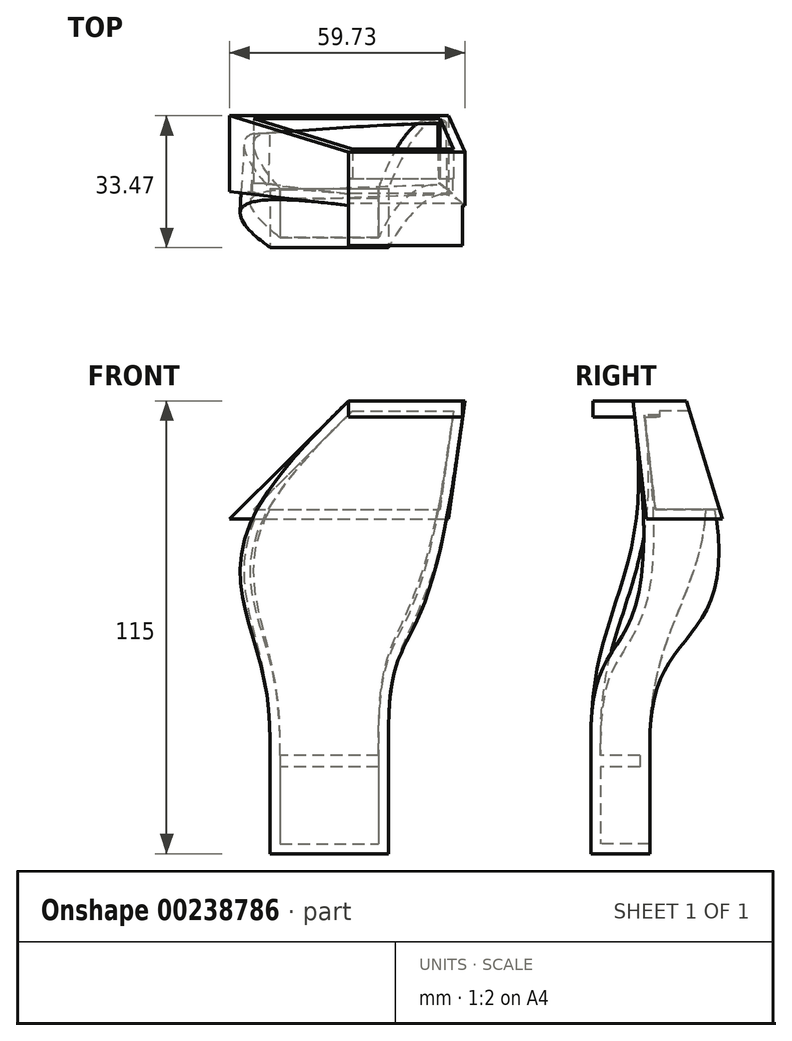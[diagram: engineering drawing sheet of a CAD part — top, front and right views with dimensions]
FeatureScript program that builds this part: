
annotation { "Feature Type Name" : "Feature", "Feature Type Description" : "" }
export const myFeature = defineFeature(function(context is Context, id is Id, definition is map)
    precondition{}
    {
        {
            var Q0;
            Q0=qCreatedBy(makeId("Top.planeOp"),FACE);
            var sketch = newSketch(context, id + "F0", { "sketchPlane" : qUnion([Q0])});
            skLineSegment(sketch, "E0.bottom", {"start": v(-29.41, -2.5) * mm, "end": v(0.59, -2.5) * mm});
            skLineSegment(sketch, "E0.top", {"start": v(-29.41, -17.5) * mm, "end": v(0.59, -17.5) * mm});
            skLineSegment(sketch, "E0.left", {"start": v(-29.41, -2.5) * mm, "end": v(-29.41, -17.5) * mm});
            skLineSegment(sketch, "E0.right", {"start": v(0.59, -2.5) * mm, "end": v(0.59, -17.5) * mm});
            skSolve(sketch);
        }
        {
            var Q0;
            Q0=makeQuery(id+"F0.imprint","IMPRINT",FACE,{"disambiguationData":[TD([[makeQuery(id+"F0.imprint","IMPRINT",EDGE,{"derivedFrom":sQuery(id+"F0.wireOp",EDGE,"E0.bottom")}),-1.0]])]});
            extrude(context, id + "F1", {"entities" : qUnion([Q0]), "depth" : 25 * mm});
        }
        {
            var Q0;
            Q0=makeQuery(id+"F1.opExtrude","CAP_FACE",FACE,{"disambiguationData":[OSD([sQuery(id+"F0.wireOp",EDGE,"E0.bottom"),sQuery(id+"F0.wireOp",EDGE,"E0.top"),sQuery(id+"F0.wireOp",EDGE,"E0.left"),sQuery(id+"F0.wireOp",EDGE,"E0.right")])],"isStart":false});
            cPlane(context, id + "F2", {"entities" : qUnion([Q0]), "cplaneType" : CPlaneType.OFFSET, "offset" : 90 * mm, "width" : 150 * mm, "height" : 150 * mm});
        }
        {
            var Q0;
            Q0=qCreatedBy(id+"F2.planeOp",FACE);
            var sketch = newSketch(context, id + "F3", { "sketchPlane" : qUnion([Q0])});
            skLineSegment(sketch, "E1.bottom", {"start": v(-9.57, 6.8) * mm, "end": v(20.02, 6.8) * mm});
            skLineSegment(sketch, "E1.top", {"start": v(-9.57, -6.78) * mm, "end": v(20.02, -6.78) * mm});
            skLineSegment(sketch, "E1.left", {"start": v(-9.57, 6.8) * mm, "end": v(-9.57, -6.78) * mm});
            skLineSegment(sketch, "E1.right", {"start": v(20.02, 6.8) * mm, "end": v(20.02, -6.78) * mm});
            skSolve(sketch);
        }
        {
            var Q0;
            Q0=makeQuery(id+"F3.imprint","IMPRINT",FACE,{"disambiguationData":[TD([[makeQuery(id+"F3.imprint","IMPRINT",EDGE,{"derivedFrom":sQuery(id+"F3.wireOp",EDGE,"E1.bottom")}),-1.0]])]});
            cPlane(context, id + "F4", {"entities" : qUnion([Q0]), "cplaneType" : CPlaneType.OFFSET, "offset" : 30 * mm, "oppositeDirection" : true, "width" : 150 * mm, "height" : 150 * mm});
        }
        {
            var Q0;
            Q0=qCreatedBy(id+"F4.planeOp",FACE);
            var sketch = newSketch(context, id + "F5", { "sketchPlane" : qUnion([Q0])});
            skLineSegment(sketch, "E2.bottom", {"start": v(-39.71, 15.96) * mm, "end": v(15.91, 15.96) * mm});
            skLineSegment(sketch, "E2.top", {"start": v(-39.71, -3.35) * mm, "end": v(15.91, -3.35) * mm});
            skLineSegment(sketch, "E2.left", {"start": v(-39.71, 15.96) * mm, "end": v(-39.71, -3.35) * mm});
            skLineSegment(sketch, "E2.right", {"start": v(15.91, 15.96) * mm, "end": v(15.91, -3.35) * mm});
            skSolve(sketch);
        }
        {
            var Q0;
            Q0=makeQuery(id+"F3.imprint","IMPRINT",FACE,{"disambiguationData":[TD([[makeQuery(id+"F3.imprint","IMPRINT",EDGE,{"derivedFrom":sQuery(id+"F3.wireOp",EDGE,"E1.bottom")}),-1.0]])]});
            var Q1;
            Q1=makeQuery(id+"F5.imprint","IMPRINT",FACE,{"disambiguationData":[TD([[makeQuery(id+"F5.imprint","IMPRINT",EDGE,{"derivedFrom":sQuery(id+"F5.wireOp",EDGE,"E2.bottom")}),-1.0]])]});
            loft(context, id + "F6", {"sheetProfilesArray" : [{ "sheetProfileEntities" : qUnion([Q0]) }, { "sheetProfileEntities" : qUnion([Q1]) }]});
        }
        {
            var Q0;
            Q0=makeQuery(id+"F6.opLoft","CAP_FACE",FACE,{"disambiguationData":[OSD([makeQuery(id+"F3.imprint","IMPRINT",FACE,{"disambiguationData":[TD([[makeQuery(id+"F3.imprint","IMPRINT",EDGE,{"derivedFrom":sQuery(id+"F3.wireOp",EDGE,"E1.bottom")}),-1.0]])]})])],"isStart":true});
            var Q1;
            Q1=makeQuery(id+"F1.opExtrude","CAP_FACE",FACE,{"disambiguationData":[OSD([sQuery(id+"F0.wireOp",EDGE,"E0.bottom"),sQuery(id+"F0.wireOp",EDGE,"E0.top"),sQuery(id+"F0.wireOp",EDGE,"E0.left"),sQuery(id+"F0.wireOp",EDGE,"E0.right")])],"isStart":false});
            var Q2;
            Q2=makeQuery(id+"F1.opExtrude","CAP_FACE",FACE,{"disambiguationData":[OSD([sQuery(id+"F0.wireOp",EDGE,"E0.bottom"),sQuery(id+"F0.wireOp",EDGE,"E0.top"),sQuery(id+"F0.wireOp",EDGE,"E0.left"),sQuery(id+"F0.wireOp",EDGE,"E0.right")])],"isStart":false});
            var Q3;
            Q3=makeQuery(id+"F6.opLoft","CAP_FACE",FACE,{"disambiguationData":[OSD([makeQuery(id+"F3.imprint","IMPRINT",FACE,{"disambiguationData":[TD([[makeQuery(id+"F3.imprint","IMPRINT",EDGE,{"derivedFrom":sQuery(id+"F3.wireOp",EDGE,"E1.bottom")}),-1.0]])]})])],"isStart":true});
            loft(context, id + "F7", {"startCondition" : LoftEndDerivativeType.MATCH_CURVATURE, "startMagnitude" : 2, "endCondition" : LoftEndDerivativeType.MATCH_CURVATURE, "endMagnitude" : 1, "sheetProfilesArray" : [{ "sheetProfileEntities" : qUnion([Q0]) }, { "sheetProfileEntities" : qUnion([Q1]) }], "wireProfilesArray" : [{ "wireProfileEntities" : qUnion([Q2]) }, { "wireProfileEntities" : qUnion([Q3]) }]});
        }
        {
            var Q0;
            Q0=makeQuery(id+"F7.opLoft","SWEPT_BODY",BODY,{"disambiguationData":[OSD([sQuery(id+"F0.wireOp",EDGE,"E0.bottom"),sQuery(id+"F0.wireOp",EDGE,"E0.top"),sQuery(id+"F0.wireOp",EDGE,"E0.left"),sQuery(id+"F0.wireOp",EDGE,"E0.right"),makeQuery(id+"F3.imprint","IMPRINT",FACE,{"disambiguationData":[TD([[makeQuery(id+"F3.imprint","IMPRINT",EDGE,{"derivedFrom":sQuery(id+"F3.wireOp",EDGE,"E1.bottom")}),-1.0]])]})])]});
            var Q1;
            Q1=makeQuery(id+"F6.opLoft","SWEPT_BODY",BODY,{"disambiguationData":[OSD([makeQuery(id+"F3.imprint","IMPRINT",FACE,{"disambiguationData":[TD([[makeQuery(id+"F3.imprint","IMPRINT",EDGE,{"derivedFrom":sQuery(id+"F3.wireOp",EDGE,"E1.bottom")}),-1.0]])]}),makeQuery(id+"F5.imprint","IMPRINT",FACE,{"disambiguationData":[TD([[makeQuery(id+"F5.imprint","IMPRINT",EDGE,{"derivedFrom":sQuery(id+"F5.wireOp",EDGE,"E2.bottom")}),-1.0]])]})])]});
            var Q2;
            Q2=makeQuery(id+"F1.opExtrude","SWEPT_BODY",BODY,{"disambiguationData":[OSD([sQuery(id+"F0.wireOp",EDGE,"E0.bottom"),sQuery(id+"F0.wireOp",EDGE,"E0.top"),sQuery(id+"F0.wireOp",EDGE,"E0.left"),sQuery(id+"F0.wireOp",EDGE,"E0.right")])]});
            booleanBodies(context, id + "F8", {"operationType" : BooleanOperationType.UNION, "tools" : qUnion([Q0, Q1, Q2])});
        }
        {
            var Q0;
            Q0=makeQuery(id+"F1.opExtrude","SWEPT_FACE",FACE,{"disambiguationData":[OSD([sQuery(id+"F0.wireOp",EDGE,"E0.bottom")])]});
            var Q1;
            Q1=makeQuery(id+"F7.opLoft","SWEPT_FACE",FACE,{"disambiguationData":[OSD([sQuery(id+"F0.wireOp",EDGE,"E0.bottom"),sQuery(id+"F0.wireOp",EDGE,"E0.left"),sQuery(id+"F0.wireOp",EDGE,"E0.right"),sQuery(id+"F3.wireOp",EDGE,"E1.bottom"),sQuery(id+"F3.wireOp",EDGE,"E1.left"),sQuery(id+"F3.wireOp",EDGE,"E1.right")])]});
            var Q2;
            Q2=makeQuery(id+"F6.opLoft","SWEPT_FACE",FACE,{"disambiguationData":[OSD([sQuery(id+"F3.wireOp",EDGE,"E1.bottom"),sQuery(id+"F3.wireOp",EDGE,"E1.left"),sQuery(id+"F3.wireOp",EDGE,"E1.right"),sQuery(id+"F5.wireOp",EDGE,"E2.bottom"),sQuery(id+"F5.wireOp",EDGE,"E2.left"),sQuery(id+"F5.wireOp",EDGE,"E2.right")])]});
            shell(context, id + "F9", {"entities" : qUnion([Q0, Q1, Q2]), "thickness" : 2.5 * mm});
        }
        {
            var Q0;
            Q0=makeQuery(id+"F9.opShell","OFFSET_VERTEX",VERTEX,{"disambiguationData":[OSD([sQuery(id+"F5.wireOp",EDGE,"E2.bottom"),sQuery(id+"F5.wireOp",EDGE,"E2.right")])]});
            var Q1;
            Q1=makeQuery(id+"F9.opShell","OFFSET_VERTEX",VERTEX,{"disambiguationData":[OSD([sQuery(id+"F3.wireOp",EDGE,"E1.bottom"),sQuery(id+"F3.wireOp",EDGE,"E1.right")]),OD(0.0)]});
            var Q2;
            Q2=makeQuery(id+"F9.opShell","OFFSET_VERTEX",VERTEX,{"disambiguationData":[OSD([sQuery(id+"F3.wireOp",EDGE,"E1.bottom"),sQuery(id+"F3.wireOp",EDGE,"E1.left")]),OD(1.0)]});
            cPlane(context, id + "F10", {"entities" : qUnion([Q0, Q1, Q2]), "cplaneType" : CPlaneType.THREE_POINT, "offset" : 60 * mm, "width" : 150 * mm, "height" : 150 * mm});
        }
        {
            var Q0;
            Q0=makeQuery(id+"F9.opShell","OFFSET_FACE",FACE,{"disambiguationData":[OSD([sQuery(id+"F0.wireOp",EDGE,"E0.top")])]});
            var sketch = newSketch(context, id + "F11", { "sketchPlane" : qUnion([Q0])});
            skLineSegment(sketch, "E3.0.0", {"start": v(1.91, 2.5) * mm, "end": v(26.91, 2.5) * mm, "construction": true});
            skLineSegment(sketch, "E3.0.1", {"start": v(26.91, 2.5) * mm, "end": v(26.91, 25) * mm, "construction": true});
            skFitSpline(sketch, "E3.0.2", {"points": [v(26.91, 25) * mm, v(18.58, 25) * mm, v(10.25, 25) * mm, v(1.91, 25) * mm], "construction": true});
            skLineSegment(sketch, "E3.0.3", {"start": v(1.91, 25) * mm, "end": v(1.91, 2.5) * mm, "construction": true});
            skLineSegment(sketch, "E4.bottom", {"start": v(1.91, 25) * mm, "end": v(26.91, 25) * mm});
            skLineSegment(sketch, "E4.top", {"start": v(1.91, 22) * mm, "end": v(26.91, 22) * mm});
            skLineSegment(sketch, "E4.left", {"start": v(1.91, 25) * mm, "end": v(1.91, 22) * mm});
            skLineSegment(sketch, "E4.right", {"start": v(26.91, 25) * mm, "end": v(26.91, 22) * mm});
            skSolve(sketch);
        }
        {
            var Q0;
            Q0=makeQuery(id+"F11.imprint","IMPRINT",FACE,{"disambiguationData":[TD([[makeQuery(id+"F11.imprint","IMPRINT",EDGE,{"derivedFrom":sQuery(id+"F11.wireOp",EDGE,"E4.bottom")}),1.0]])]});
            extrude(context, id + "F12", {"entities" : qUnion([Q0]), "operationType" : NewBodyOperationType.ADD, "depth" : 10 * mm});
        }
        {
            var Q0;
            Q0=qCreatedBy(makeId("Front.planeOp"),FACE);
            var sketch = newSketch(context, id + "F13", { "sketchPlane" : qUnion([Q0])});
            skFitSpline(sketch, "E5.0.0", {"points": [v(-9.57, 115) * mm, v(-31.26, 93.41) * mm, v(-52.96, 71.82) * mm, v(-29.41, 60.19) * mm, v(-29.41, 42.6) * mm, v(-29.41, 25) * mm], "construction": true});
            skLineSegment(sketch, "E5.0.1", {"start": v(-29.41, 25) * mm, "end": v(0.59, 25) * mm, "construction": true});
            skFitSpline(sketch, "E5.0.2", {"points": [v(0.59, 25) * mm, v(0.59, 42.6) * mm, v(0.59, 60.19) * mm, v(11.75, 54.54) * mm, v(15.88, 84.77) * mm, v(20.02, 115) * mm], "construction": true});
            skLineSegment(sketch, "E5.0.3", {"start": v(20.02, 115) * mm, "end": v(-9.57, 115) * mm, "construction": true});
            skLineSegment(sketch, "E6", {"start": v(-9.57, 115) * mm, "end": v(43.43, 115) * mm, "construction": true});
            skLineSegment(sketch, "E7.bottom", {"start": v(-9.57, 115) * mm, "end": v(19.47, 115) * mm});
            skLineSegment(sketch, "E7.top", {"start": v(-9.57, 111) * mm, "end": v(19.47, 111) * mm});
            skLineSegment(sketch, "E7.left", {"start": v(-9.57, 115) * mm, "end": v(-9.57, 111) * mm});
            skLineSegment(sketch, "E7.right", {"start": v(19.47, 115) * mm, "end": v(19.47, 111) * mm});
            skSolve(sketch);
        }
        {
            var Q0;
            Q0 = qSketchRegion(id + "F13", true);
            extrude(context, id + "F14", {"entities" : qUnion([Q0]), "operationType" : NewBodyOperationType.ADD, "depth" : 17 * mm});
        }
    });
